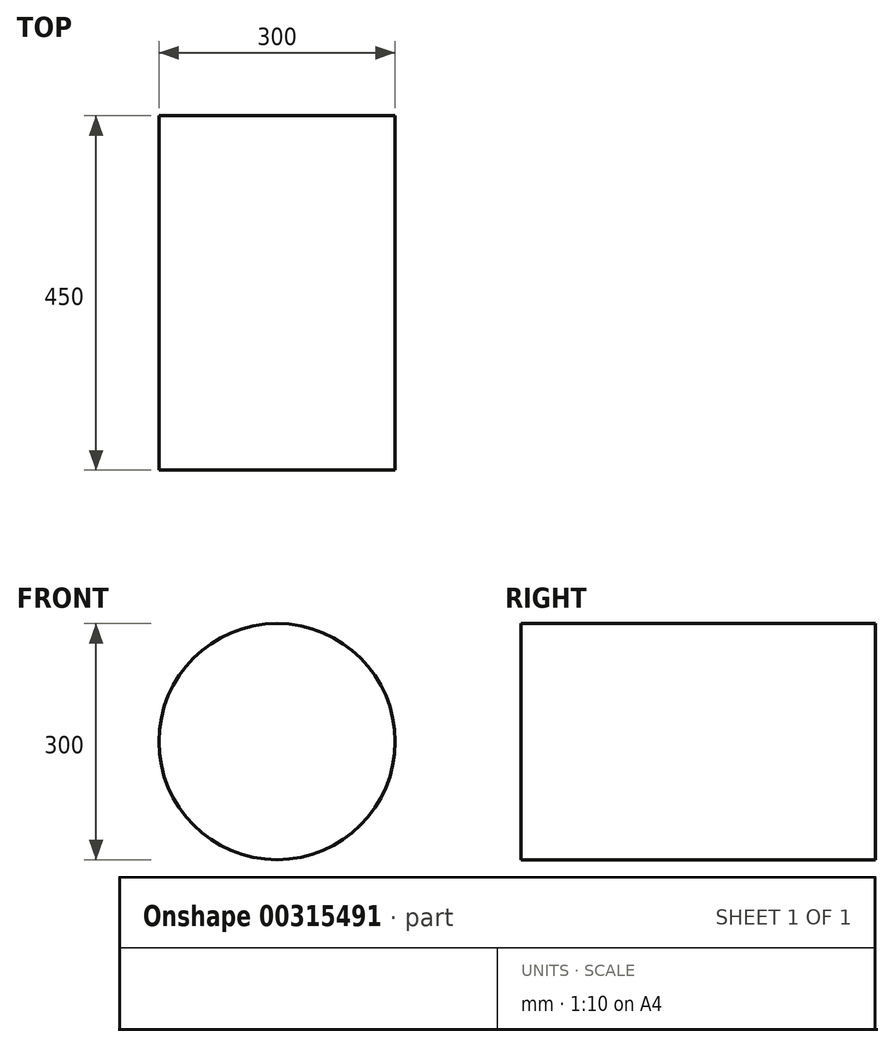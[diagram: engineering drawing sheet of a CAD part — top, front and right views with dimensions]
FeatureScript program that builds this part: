
annotation { "Feature Type Name" : "Feature", "Feature Type Description" : "" }
export const myFeature = defineFeature(function(context is Context, id is Id, definition is map)
    precondition{}
    {
        {
            var Q0;
            Q0=qCreatedBy(makeId("Front.planeOp"),FACE);
            var sketch = newSketch(context, id + "F0", { "sketchPlane" : qUnion([Q0])});
            skCircle(sketch, "E0", {"center": v(0, 0) * mm, "radius": 150 * mm});
            skSolve(sketch);
        }
        {
            var Q0;
            Q0=makeQuery(id+"F0.imprint","IMPRINT",FACE,{"disambiguationData":[TD([[makeQuery(id+"F0.imprint","IMPRINT",EDGE,{"derivedFrom":sQuery(id+"F0.wireOp",EDGE,"E0")}),1.0]])]});
            extrude(context, id + "F1", {"entities" : qUnion([Q0]), "endBound" : BoundingType.SYMMETRIC, "depth" : 450 * mm, "hasSecondDirection" : true, "secondDirectionOppositeDirection" : true, "secondDirectionDepth" : 25 * mm});
        }
    });
